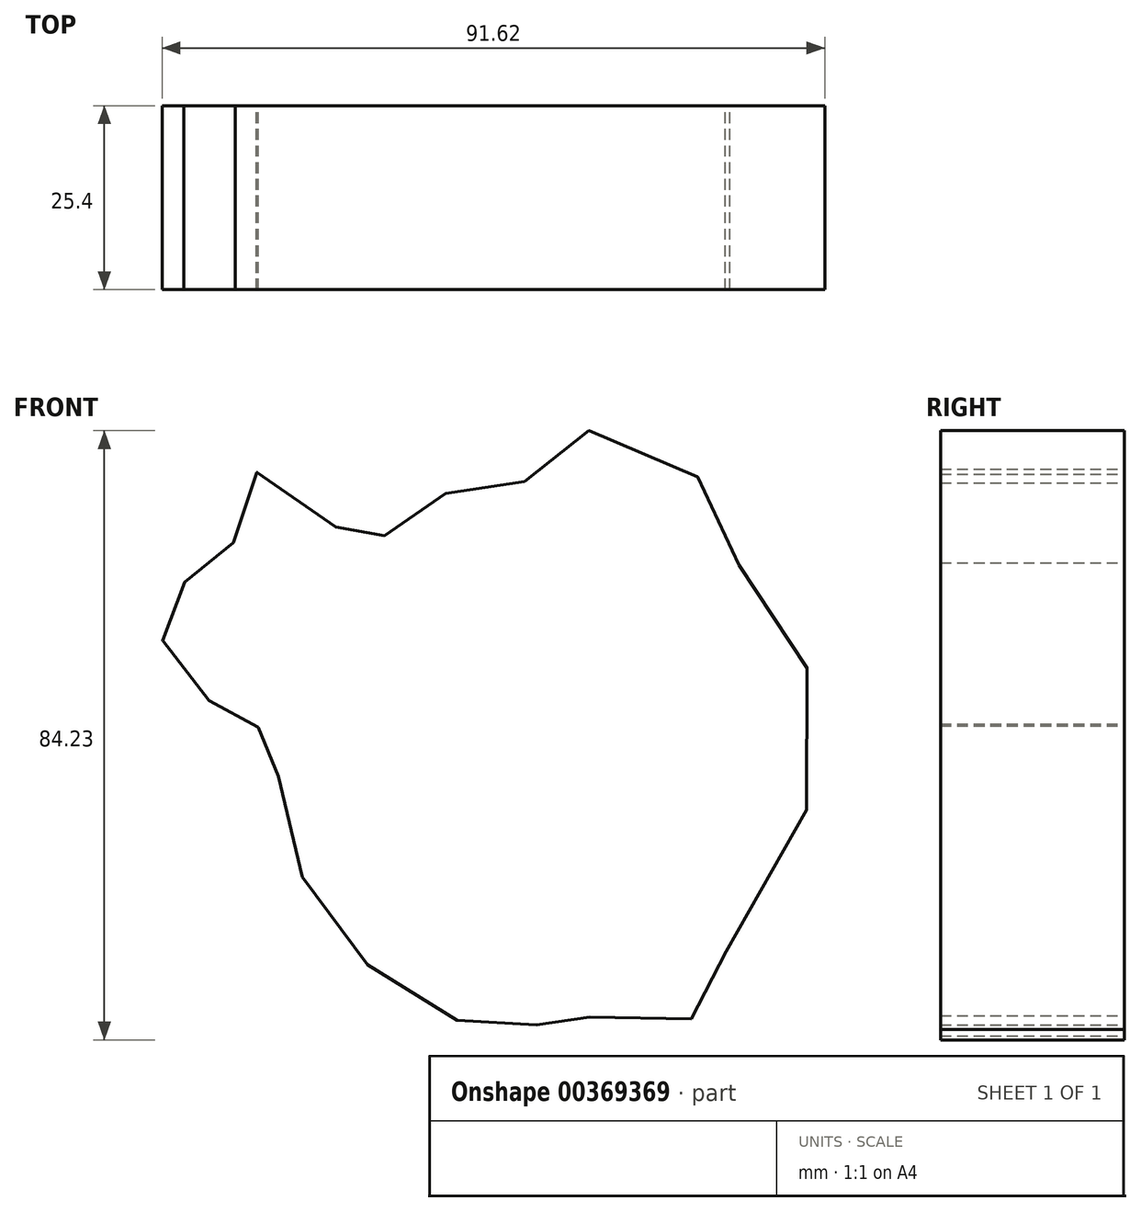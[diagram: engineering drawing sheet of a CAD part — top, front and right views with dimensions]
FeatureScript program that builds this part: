
annotation { "Feature Type Name" : "Feature", "Feature Type Description" : "" }
export const myFeature = defineFeature(function(context is Context, id is Id, definition is map)
    precondition{}
    {
        {
            var Q0;
            Q0=qCreatedBy(makeId("Front.planeOp"),FACE);
            var sketch = newSketch(context, id + "F0", { "sketchPlane" : qUnion([Q0])});
            skFitSpline(sketch, "E0", {"points": [v(-19.28, -33.1) * mm, v(-26.77, -23.89) * mm, v(-31.37, -11.22) * mm, v(-32.23, -5.47) * mm, v(-34.54, -3.74) * mm, v(-34.54, 0) * mm, v(-37.7, 0) * mm, v(-40.87, 3.17) * mm, v(-46.34, 6.62) * mm, v(-47.2, 12.95) * mm, v(-44.9, 15.25) * mm, v(-44.32, 20.43) * mm, v(-40.58, 21.87) * mm, v(-37.7, 25.9) * mm, v(-37.13, 32.23) * mm, v(-32.23, 35.4) * mm, v(-23.6, 27.34) * mm, v(-21.3, 22.45) * mm, v(-13.81, 28.78) * mm, v(-9.79, 29.93) * mm, v(-6.33, 34.54) * mm, v(2.3, 33.67) * mm, v(5.76, 39.14) * mm, v(18.13, 39.43) * mm, v(28.2, 31.95) * mm, v(31.66, 23.02) * mm, v(40, 10.65) * mm, v(42.88, -8.06) * mm, v(30.22, -31.66) * mm, v(30.8, -34.82) * mm, v(21.3, -42.02) * mm, v(11.51, -40.3) * mm, v(8.63, -43.46) * mm, v(4.32, -41.44) * mm, v(0, -42.88) * mm, v(-10.36, -38.85) * mm, v(-19.28, -33.1) * mm]});
            skSolve(sketch);
        }
        {
            var Q0;
            Q0 = qSketchRegion(id + "F0", true);
            extrude(context, id + "F1", {"entities" : qUnion([Q0]), "depth" : 25.4 * mm});
        }
    });
